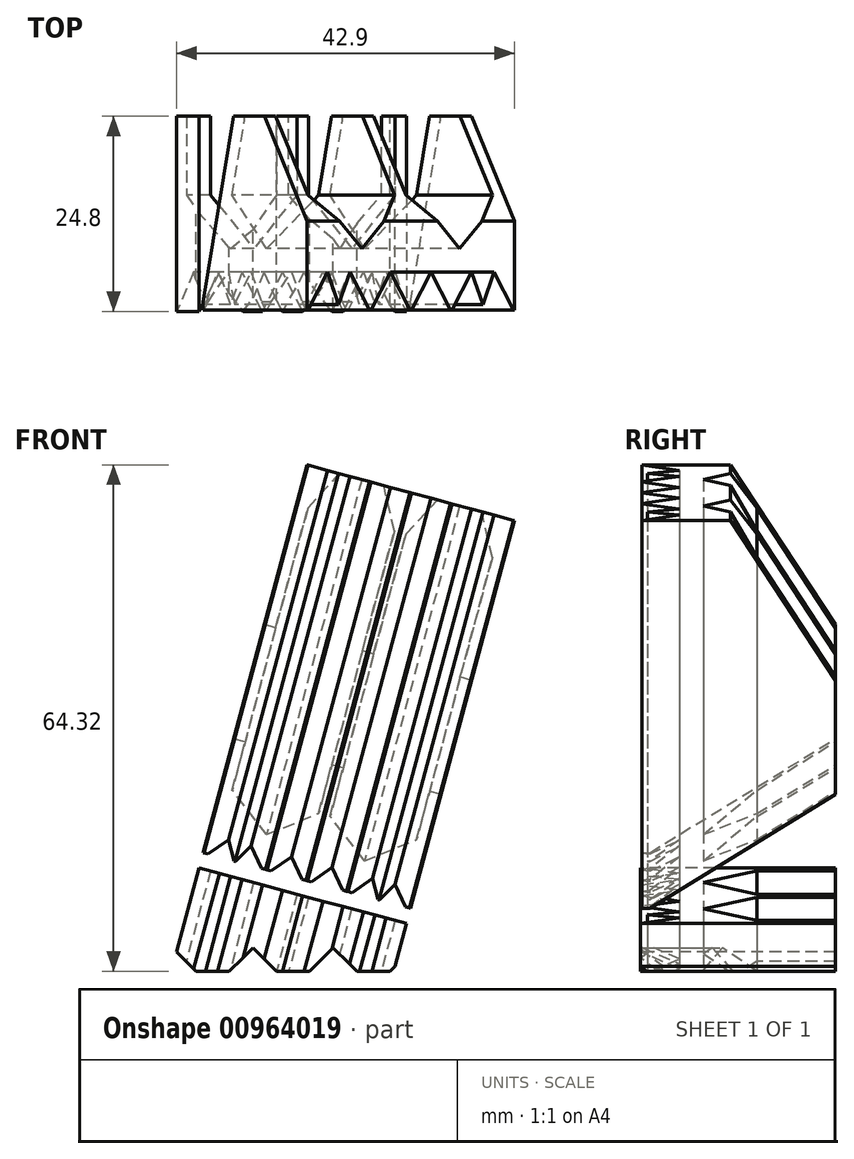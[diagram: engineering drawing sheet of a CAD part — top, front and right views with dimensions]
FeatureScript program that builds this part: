
annotation { "Feature Type Name" : "Feature", "Feature Type Description" : "" }
export const myFeature = defineFeature(function(context is Context, id is Id, definition is map)
    precondition{}
    {
        {
            assignVariable(context, id + "F0", {"variableType" : VariableType.LENGTH, "name" : "l", "lengthValue" : 35.5 * mm});
        }
        {
            assignVariable(context, id + "F1", {"variableType" : VariableType.LENGTH, "name" : "b", "lengthValue" : 23.6 * mm});
        }
        {
            assignVariable(context, id + "F2", {"variableType" : VariableType.LENGTH, "name" : "h", "lengthValue" : 50 * mm});
        }
        {
            var Q0;
            Q0=qCreatedBy(makeId("Front.planeOp"),FACE);
            var sketch = newSketch(context, id + "F3", { "sketchPlane" : qUnion([Q0])});
            skLineSegment(sketch, "E0", {"start": v(-22.52, 0) * mm, "end": v(-6.84, 58.52) * mm});
            skLineSegment(sketch, "E1", {"start": v(-6.84, 58.52) * mm, "end": v(35.18, 47.26) * mm});
            skLineSegment(sketch, "E2", {"start": v(35.18, 47.26) * mm, "end": v(22.52, 0) * mm});
            skLineSegment(sketch, "E3", {"start": v(22.52, 0) * mm, "end": v(22.52, -5) * mm});
            skLineSegment(sketch, "E4", {"start": v(15.31, -2) * mm, "end": v(12.31, -5) * mm});
            skLineSegment(sketch, "E5", {"start": v(15.31, -2) * mm, "end": v(18.31, -5) * mm});
            skLineSegment(sketch, "E6", {"start": v(14.17, 52.9) * mm, "end": v(0, 0) * mm, "construction": true});
            skLineSegment(sketch, "E7", {"start": v(-2.97, 57.48) * mm, "end": v(-15.91, 9.19) * mm, "construction": true});
            skLineSegment(sketch, "E8", {"start": v(-15.91, 9.19) * mm, "end": v(18.38, 0) * mm, "construction": true});
            skLineSegment(sketch, "E9", {"start": v(18.38, 0) * mm, "end": v(31.32, 48.3) * mm, "construction": true});
            skLineSegment(sketch, "E10", {"start": v(18.31, -5) * mm, "end": v(22.52, -5) * mm});
            skLineSegment(sketch, "E11", {"start": v(12.31, -5) * mm, "end": v(8.1, -5) * mm});
            skLineSegment(sketch, "E12.1.0.0", {"start": v(2.1, -5) * mm, "end": v(-2.1, -5) * mm});
            skLineSegment(sketch, "E12.1.0.1", {"start": v(5.1, -2) * mm, "end": v(8.1, -5) * mm});
            skLineSegment(sketch, "E12.1.0.2", {"start": v(5.1, -2) * mm, "end": v(2.1, -5) * mm});
            skLineSegment(sketch, "E12.2.0.0", {"start": v(-8.1, -5) * mm, "end": v(-12.31, -5) * mm});
            skLineSegment(sketch, "E12.2.0.1", {"start": v(-5.1, -2) * mm, "end": v(-2.1, -5) * mm});
            skLineSegment(sketch, "E12.2.0.2", {"start": v(-5.1, -2) * mm, "end": v(-8.1, -5) * mm});
            skLineSegment(sketch, "E12.3.0.0", {"start": v(-18.31, -5) * mm, "end": v(-22.52, -5) * mm});
            skLineSegment(sketch, "E12.3.0.1", {"start": v(-15.31, -2) * mm, "end": v(-12.31, -5) * mm});
            skLineSegment(sketch, "E12.3.0.2", {"start": v(-15.31, -2) * mm, "end": v(-18.31, -5) * mm});
            skLineSegment(sketch, "E12.direction1", {"start": v(8.1, -5) * mm, "end": v(-2.1, -5) * mm, "construction": true});
            skLineSegment(sketch, "E13", {"start": v(-22.52, -5) * mm, "end": v(-22.52, 0) * mm});
            skPoint(sketch, "E14", {"position": v(24.85, 24.15) * mm});
            skSolve(sketch);
        }
        {
            var Q0;
            Q0=sQuery(id+"F3.wireOp",EDGE,"E9");
            var Q1;
            Q1=sQuery(id+"F3.wireOp",VERTEX,"E14");
            cPlane(context, id + "F4", {"entities" : qUnion([Q0, Q1]), "cplaneType" : CPlaneType.LINE_POINT, "offset" : 25 * mm, "width" : 150 * mm, "height" : 150 * mm});
        }
        {
            var Q0;
            Q0=qCreatedBy(id+"F4.planeOp",FACE);
            var sketch = newSketch(context, id + "F5", { "sketchPlane" : qUnion([Q0])});
            skLineSegment(sketch, "E15.bottom", {"start": v(-17.75, 11.8) * mm, "end": v(17.75, 11.8) * mm, "construction": true});
            skLineSegment(sketch, "E15.top", {"start": v(-17.75, -11.8) * mm, "end": v(17.75, -11.8) * mm, "construction": true});
            skLineSegment(sketch, "E15.left", {"start": v(-17.75, 11.8) * mm, "end": v(-17.75, -11.8) * mm, "construction": true});
            skLineSegment(sketch, "E15.right", {"start": v(17.75, 11.8) * mm, "end": v(17.75, -11.8) * mm, "construction": true});
            skLineSegment(sketch, "E16.0", {"start": v(-18.35, 12.4) * mm, "end": v(18.35, 12.4) * mm});
            skLineSegment(sketch, "E16.1", {"start": v(-18.35, 12.4) * mm, "end": v(-18.35, -12.4) * mm});
            skLineSegment(sketch, "E16.2", {"start": v(-18.35, -12.4) * mm, "end": v(18.35, -12.4) * mm});
            skLineSegment(sketch, "E16.3", {"start": v(18.35, 12.4) * mm, "end": v(18.35, -12.4) * mm});
            skLineSegment(sketch, "E17", {"start": v(8.86, 12.4) * mm, "end": v(9.38, 11.5) * mm});
            skLineSegment(sketch, "E18", {"start": v(9.38, 11.5) * mm, "end": v(9.58, 11.5) * mm});
            skLineSegment(sketch, "E19", {"start": v(9.58, 11.5) * mm, "end": v(10.1, 12.4) * mm});
            skLineSegment(sketch, "E20", {"start": v(10.1, 12.4) * mm, "end": v(8.86, 12.4) * mm});
            skLineSegment(sketch, "E21", {"start": v(9.48, 12.4) * mm, "end": v(9.48, 11.5) * mm, "construction": true});
            skLineSegment(sketch, "E22.1.0", {"start": v(18.35, 7.12) * mm, "end": v(17.45, 6.6) * mm});
            skLineSegment(sketch, "E22.1.1", {"start": v(18.35, 6.5) * mm, "end": v(17.45, 6.5) * mm, "construction": true});
            skLineSegment(sketch, "E22.1.2", {"start": v(18.35, 5.88) * mm, "end": v(18.35, 7.12) * mm});
            skLineSegment(sketch, "E22.1.3", {"start": v(17.45, 6.4) * mm, "end": v(18.35, 5.88) * mm});
            skLineSegment(sketch, "E22.1.4", {"start": v(17.45, 6.6) * mm, "end": v(17.45, 6.4) * mm});
            skPoint(sketch, "E22.center", {"position": v(10.96, 5.01) * mm});
            skLineSegment(sketch, "E22.anchor1", {"start": v(10.96, 5.01) * mm, "end": v(9.48, 11.5) * mm, "construction": true});
            skLineSegment(sketch, "E22.anchor2", {"start": v(10.96, 5.01) * mm, "end": v(17.45, 6.5) * mm, "construction": true});
            skLineSegment(sketch, "E23.MirrorCS", {"start": v(9.38, -11.5) * mm, "end": v(9.58, -11.5) * mm});
            skLineSegment(sketch, "E24.MirrorCS", {"start": v(9.58, -11.5) * mm, "end": v(10.1, -12.4) * mm});
            skLineSegment(sketch, "E25.MirrorCS", {"start": v(10.1, -12.4) * mm, "end": v(8.86, -12.4) * mm});
            skLineSegment(sketch, "E26.MirrorCS", {"start": v(8.86, -12.4) * mm, "end": v(9.38, -11.5) * mm});
            skLineSegment(sketch, "E27.MirrorCS", {"start": v(9.48, -12.4) * mm, "end": v(9.48, -11.5) * mm, "construction": true});
            skLineSegment(sketch, "E28.MirrorCS", {"start": v(17.45, -6.6) * mm, "end": v(17.45, -6.4) * mm});
            skLineSegment(sketch, "E29.MirrorCS", {"start": v(18.35, -5.88) * mm, "end": v(18.35, -7.12) * mm});
            skLineSegment(sketch, "E30.MirrorCS", {"start": v(18.35, -6.5) * mm, "end": v(17.45, -6.5) * mm, "construction": true});
            skLineSegment(sketch, "E31.MirrorCS", {"start": v(18.35, -7.12) * mm, "end": v(17.45, -6.6) * mm});
            skLineSegment(sketch, "E32.MirrorCS", {"start": v(17.45, -6.4) * mm, "end": v(18.35, -5.88) * mm});
            skLineSegment(sketch, "E33", {"start": v(0, 11.8) * mm, "end": v(0, -11.8) * mm, "construction": true});
            skLineSegment(sketch, "E34.MirrorCS", {"start": v(-9.38, 11.5) * mm, "end": v(-9.58, 11.5) * mm});
            skLineSegment(sketch, "E35.MirrorCS", {"start": v(-9.57, 11.5) * mm, "end": v(-10.1, 12.4) * mm});
            skLineSegment(sketch, "E36.MirrorCS", {"start": v(-8.86, 12.4) * mm, "end": v(-9.38, 11.5) * mm});
            skLineSegment(sketch, "E37.MirrorCS", {"start": v(-9.47, 12.4) * mm, "end": v(-9.47, 11.5) * mm, "construction": true});
            skLineSegment(sketch, "E38.MirrorCS", {"start": v(-10.1, 12.4) * mm, "end": v(-8.86, 12.4) * mm});
            skLineSegment(sketch, "E39.MirrorCS", {"start": v(-17.45, 6.6) * mm, "end": v(-17.45, 6.4) * mm});
            skLineSegment(sketch, "E40.MirrorCS", {"start": v(-17.45, 6.4) * mm, "end": v(-18.35, 5.88) * mm});
            skLineSegment(sketch, "E41.MirrorCS", {"start": v(-18.35, 7.12) * mm, "end": v(-17.45, 6.6) * mm});
            skLineSegment(sketch, "E42.MirrorCS", {"start": v(-17.45, -6.6) * mm, "end": v(-17.45, -6.4) * mm});
            skLineSegment(sketch, "E43.MirrorCS", {"start": v(-17.45, -6.4) * mm, "end": v(-18.35, -5.88) * mm});
            skLineSegment(sketch, "E44.MirrorCS", {"start": v(-18.35, -7.12) * mm, "end": v(-17.45, -6.6) * mm});
            skLineSegment(sketch, "E45.MirrorCS", {"start": v(-18.35, 6.5) * mm, "end": v(-17.45, 6.5) * mm, "construction": true});
            skLineSegment(sketch, "E46.MirrorCS", {"start": v(-18.35, 5.88) * mm, "end": v(-18.35, 7.12) * mm});
            skLineSegment(sketch, "E47.MirrorCS", {"start": v(-18.35, -5.88) * mm, "end": v(-18.35, -7.12) * mm});
            skLineSegment(sketch, "E48.MirrorCS", {"start": v(-18.35, -6.5) * mm, "end": v(-17.45, -6.5) * mm, "construction": true});
            skLineSegment(sketch, "E49.MirrorCS", {"start": v(-9.38, -11.5) * mm, "end": v(-9.58, -11.5) * mm});
            skLineSegment(sketch, "E50.MirrorCS", {"start": v(-9.57, -11.5) * mm, "end": v(-10.1, -12.4) * mm});
            skLineSegment(sketch, "E51.MirrorCS", {"start": v(-9.48, -12.4) * mm, "end": v(-9.48, -11.5) * mm, "construction": true});
            skLineSegment(sketch, "E52.MirrorCS", {"start": v(-8.86, -12.4) * mm, "end": v(-9.38, -11.5) * mm});
            skLineSegment(sketch, "E53.MirrorCS", {"start": v(-10.1, -12.4) * mm, "end": v(-8.86, -12.4) * mm});
            skSolve(sketch);
        }
        {
            var Q0;
            Q0 = qSketchRegion(id + "F3", true);
            extrude(context, id + "F6", {"entities" : qUnion([Q0]), "depth" : getVariable(context, 'b') + 2 * 4 * mm, "offsetDistance" : 25 * mm, "symmetric" : true});
        }
        {
            var Q0;
            Q0 = qSketchRegion(id + "F5", true);
            extrude(context, id + "F7", {"entities" : qUnion([Q0]), "operationType" : NewBodyOperationType.REMOVE, "oppositeDirection" : true, "depth" : getVariable(context, 'h'), "offsetDistance" : 25 * mm, "symmetric" : true});
        }
        {
            var Q0;
            Q0=makeQuery(id+"F5.imprint","IMPRINT",FACE,{"disambiguationData":[TD([[makeQuery(id+"F5.imprint","IMPRINT",EDGE,{"derivedFrom":sQuery(id+"F5.wireOp",EDGE,"E49.MirrorCS")}),1.0]])]});
            var Q1;
            Q1=makeQuery(id+"F5.imprint","IMPRINT",FACE,{"disambiguationData":[TD([[makeQuery(id+"F5.imprint","IMPRINT",EDGE,{"derivedFrom":sQuery(id+"F5.wireOp",EDGE,"E23.MirrorCS")}),-1.0]])]});
            var Q2;
            Q2=makeQuery(id+"F5.imprint","IMPRINT",FACE,{"disambiguationData":[TD([[makeQuery(id+"F5.imprint","IMPRINT",EDGE,{"derivedFrom":sQuery(id+"F5.wireOp",EDGE,"E28.MirrorCS")}),-1.0]])]});
            var Q3;
            Q3=makeQuery(id+"F5.imprint","IMPRINT",FACE,{"disambiguationData":[TD([[makeQuery(id+"F5.imprint","IMPRINT",EDGE,{"derivedFrom":sQuery(id+"F5.wireOp",EDGE,"E42.MirrorCS")}),1.0]])]});
            var Q4;
            Q4=makeQuery(id+"F5.imprint","IMPRINT",FACE,{"disambiguationData":[TD([[makeQuery(id+"F5.imprint","IMPRINT",EDGE,{"derivedFrom":sQuery(id+"F5.wireOp",EDGE,"E39.MirrorCS")}),-1.0]])]});
            var Q5;
            Q5=makeQuery(id+"F5.imprint","IMPRINT",FACE,{"disambiguationData":[TD([[makeQuery(id+"F5.imprint","IMPRINT",EDGE,{"derivedFrom":sQuery(id+"F5.wireOp",EDGE,"E34.MirrorCS")}),-1.0]])]});
            var Q6;
            {var subQ0=sQuery(id+"F5.wireOp",EDGE,"E17");Q6=makeQuery(id+"F5.imprint","IMPRINT",FACE,{"disambiguationData":[TD([[makeQuery(id+"F5.imprint","IMPRINT",EDGE,{"derivedFrom":subQ0}),1.0]])]});}
            var Q7;
            {var subQ2=sQuery(id+"F5.wireOp",EDGE,"E22.1.0");Q7=makeQuery(id+"F5.imprint","IMPRINT",FACE,{"disambiguationData":[TD([[makeQuery(id+"F5.imprint","IMPRINT",EDGE,{"derivedFrom":subQ2}),1.0]])]});}
            extrude(context, id + "F8", {"entities" : qUnion([Q0, Q1, Q2, Q3, Q4, Q5, Q6, Q7]), "operationType" : NewBodyOperationType.ADD, "depth" : getVariable(context, 'h') / 3, "offsetDistance" : 25 * mm, "hasSecondDirection" : true, "secondDirectionOppositeDirection" : true, "secondDirectionDepth" : getVariable(context, 'h') / 2 - 2 * mm});
        }
        {
            var Q0;
            Q0=makeQuery(id+"F8.opExtrude","CAP_EDGE",EDGE,{"disambiguationData":[OSD([sQuery(id+"F5.wireOp",EDGE,"E34.MirrorCS")])],"isStart":false});
            var Q1;
            Q1=makeQuery(id+"F8.opExtrude","CAP_EDGE",EDGE,{"disambiguationData":[OSD([sQuery(id+"F5.wireOp",EDGE,"E28.MirrorCS")])],"isStart":false});
            var Q2;
            Q2=makeQuery(id+"F8.opExtrude","CAP_EDGE",EDGE,{"disambiguationData":[OSD([sQuery(id+"F5.wireOp",EDGE,"E23.MirrorCS")])],"isStart":false});
            var Q3;
            Q3=makeQuery(id+"F8.opExtrude","CAP_EDGE",EDGE,{"disambiguationData":[OSD([sQuery(id+"F5.wireOp",EDGE,"E39.MirrorCS")])],"isStart":false});
            chamfer(context, id + "F9", {"entities" : qUnion([Q0, Q1, Q2, Q3]), "chamferType" : ChamferType.OFFSET_ANGLE, "width" : 3 * mm, "oppositeDirection" : false, "angle" : 20 * degree});
        }
        {
            var Q0;
            Q0=makeQuery(id+"F8.opExtrude","CAP_EDGE",EDGE,{"disambiguationData":[OSD([sQuery(id+"F5.wireOp",EDGE,"E42.MirrorCS")])],"isStart":false});
            var Q1;
            Q1=makeQuery(id+"F8.opExtrude","CAP_EDGE",EDGE,{"disambiguationData":[OSD([sQuery(id+"F5.wireOp",EDGE,"E49.MirrorCS")])],"isStart":false});
            var Q2;
            Q2=makeQuery(id+"F8.opExtrude","CAP_EDGE",EDGE,{"disambiguationData":[OSD([sQuery(id+"F5.wireOp",EDGE,"E18")])],"isStart":false});
            var Q3;
            Q3=makeQuery(id+"F8.opExtrude","CAP_EDGE",EDGE,{"disambiguationData":[OSD([sQuery(id+"F5.wireOp",EDGE,"E22.1.4")])],"isStart":false});
            chamfer(context, id + "F10", {"entities" : qUnion([Q0, Q1, Q2, Q3]), "chamferType" : ChamferType.OFFSET_ANGLE, "width" : 1 * mm, "oppositeDirection" : false, "angle" : 70 * degree, "tangentPropagation" : true});
        }
        {
            var Q0;
            Q0=makeQuery(id+"F6.opExtrude","SWEPT_FACE",FACE,{"disambiguationData":[OSD([sQuery(id+"F3.wireOp",EDGE,"E1")])]});
            chamfer(context, id + "F11", {"entities" : qUnion([Q0]), "width" : 1 * mm, "tangentPropagation" : true});
        }
        {
            var Q0;
            Q0=makeQuery(id+"F6.opExtrude","CAP_EDGE",EDGE,{"disambiguationData":[OSD([sQuery(id+"F3.wireOp",EDGE,"E0")])],"isStart":false});
            var Q1;
            Q1=makeQuery(id+"F6.opExtrude","CAP_EDGE",EDGE,{"disambiguationData":[OSD([sQuery(id+"F3.wireOp",EDGE,"E0")])],"isStart":true});
            var Q2;
            Q2=makeQuery(id+"F6.opExtrude","CAP_EDGE",EDGE,{"disambiguationData":[OSD([sQuery(id+"F3.wireOp",EDGE,"E2")])],"isStart":false});
            var Q3;
            Q3=makeQuery(id+"F6.opExtrude","CAP_EDGE",EDGE,{"disambiguationData":[OSD([sQuery(id+"F3.wireOp",EDGE,"E2")])],"isStart":true});
            var Q4;
            Q4=makeQuery(id+"F6.opExtrude","CAP_EDGE",EDGE,{"disambiguationData":[OSD([sQuery(id+"F3.wireOp",EDGE,"E3")])],"isStart":false});
            var Q5;
            Q5=makeQuery(id+"F6.opExtrude","CAP_EDGE",EDGE,{"disambiguationData":[OSD([sQuery(id+"F3.wireOp",EDGE,"E3")])],"isStart":true});
            var Q6;
            Q6=makeQuery(id+"F6.opExtrude","CAP_EDGE",EDGE,{"disambiguationData":[OSD([sQuery(id+"F3.wireOp",EDGE,"E13")])],"isStart":false});
            var Q7;
            Q7=makeQuery(id+"F6.opExtrude","CAP_EDGE",EDGE,{"disambiguationData":[OSD([sQuery(id+"F3.wireOp",EDGE,"E13")])],"isStart":true});
            var Q8;
            Q8=makeQuery(id+"F6.opExtrude","CAP_EDGE",EDGE,{"disambiguationData":[OSD([sQuery(id+"F3.wireOp",EDGE,"E12.3.0.0")])],"isStart":false});
            var Q9;
            Q9=makeQuery(id+"F6.opExtrude","CAP_EDGE",EDGE,{"disambiguationData":[OSD([sQuery(id+"F3.wireOp",EDGE,"E12.2.0.0")])],"isStart":false});
            var Q10;
            Q10=makeQuery(id+"F6.opExtrude","CAP_EDGE",EDGE,{"disambiguationData":[OSD([sQuery(id+"F3.wireOp",EDGE,"E12.3.0.1")])],"isStart":false});
            var Q11;
            Q11=makeQuery(id+"F6.opExtrude","CAP_EDGE",EDGE,{"disambiguationData":[OSD([sQuery(id+"F3.wireOp",EDGE,"E12.3.0.2")])],"isStart":false});
            var Q12;
            Q12=makeQuery(id+"F6.opExtrude","CAP_EDGE",EDGE,{"disambiguationData":[OSD([sQuery(id+"F3.wireOp",EDGE,"E12.2.0.2")])],"isStart":false});
            var Q13;
            Q13=makeQuery(id+"F6.opExtrude","CAP_EDGE",EDGE,{"disambiguationData":[OSD([sQuery(id+"F3.wireOp",EDGE,"E12.2.0.1")])],"isStart":false});
            var Q14;
            Q14=makeQuery(id+"F6.opExtrude","CAP_EDGE",EDGE,{"disambiguationData":[OSD([sQuery(id+"F3.wireOp",EDGE,"E12.1.0.0")])],"isStart":false});
            var Q15;
            Q15=makeQuery(id+"F6.opExtrude","CAP_EDGE",EDGE,{"disambiguationData":[OSD([sQuery(id+"F3.wireOp",EDGE,"E12.1.0.2")])],"isStart":false});
            var Q16;
            Q16=makeQuery(id+"F6.opExtrude","CAP_EDGE",EDGE,{"disambiguationData":[OSD([sQuery(id+"F3.wireOp",EDGE,"E12.1.0.1")])],"isStart":false});
            var Q17;
            Q17=makeQuery(id+"F6.opExtrude","CAP_EDGE",EDGE,{"disambiguationData":[OSD([sQuery(id+"F3.wireOp",EDGE,"E11")])],"isStart":false});
            var Q18;
            Q18=makeQuery(id+"F6.opExtrude","CAP_EDGE",EDGE,{"disambiguationData":[OSD([sQuery(id+"F3.wireOp",EDGE,"E4")])],"isStart":false});
            var Q19;
            Q19=makeQuery(id+"F6.opExtrude","CAP_EDGE",EDGE,{"disambiguationData":[OSD([sQuery(id+"F3.wireOp",EDGE,"E5")])],"isStart":false});
            var Q20;
            Q20=makeQuery(id+"F6.opExtrude","CAP_EDGE",EDGE,{"disambiguationData":[OSD([sQuery(id+"F3.wireOp",EDGE,"E10")])],"isStart":false});
            var Q21;
            Q21=makeQuery(id+"F6.opExtrude","CAP_EDGE",EDGE,{"disambiguationData":[OSD([sQuery(id+"F3.wireOp",EDGE,"E10")])],"isStart":true});
            var Q22;
            Q22=makeQuery(id+"F6.opExtrude","CAP_EDGE",EDGE,{"disambiguationData":[OSD([sQuery(id+"F3.wireOp",EDGE,"E5")])],"isStart":true});
            var Q23;
            Q23=makeQuery(id+"F6.opExtrude","CAP_EDGE",EDGE,{"disambiguationData":[OSD([sQuery(id+"F3.wireOp",EDGE,"E4")])],"isStart":true});
            var Q24;
            Q24=makeQuery(id+"F6.opExtrude","CAP_EDGE",EDGE,{"disambiguationData":[OSD([sQuery(id+"F3.wireOp",EDGE,"E11")])],"isStart":true});
            var Q25;
            Q25=makeQuery(id+"F6.opExtrude","CAP_EDGE",EDGE,{"disambiguationData":[OSD([sQuery(id+"F3.wireOp",EDGE,"E12.1.0.1")])],"isStart":true});
            var Q26;
            Q26=makeQuery(id+"F6.opExtrude","CAP_EDGE",EDGE,{"disambiguationData":[OSD([sQuery(id+"F3.wireOp",EDGE,"E12.1.0.2")])],"isStart":true});
            var Q27;
            Q27=makeQuery(id+"F6.opExtrude","CAP_EDGE",EDGE,{"disambiguationData":[OSD([sQuery(id+"F3.wireOp",EDGE,"E12.1.0.0")])],"isStart":true});
            var Q28;
            Q28=makeQuery(id+"F6.opExtrude","CAP_EDGE",EDGE,{"disambiguationData":[OSD([sQuery(id+"F3.wireOp",EDGE,"E12.2.0.1")])],"isStart":true});
            var Q29;
            Q29=makeQuery(id+"F6.opExtrude","CAP_EDGE",EDGE,{"disambiguationData":[OSD([sQuery(id+"F3.wireOp",EDGE,"E12.2.0.2")])],"isStart":true});
            var Q30;
            Q30=makeQuery(id+"F6.opExtrude","CAP_EDGE",EDGE,{"disambiguationData":[OSD([sQuery(id+"F3.wireOp",EDGE,"E12.2.0.0")])],"isStart":true});
            var Q31;
            Q31=makeQuery(id+"F6.opExtrude","CAP_EDGE",EDGE,{"disambiguationData":[OSD([sQuery(id+"F3.wireOp",EDGE,"E12.3.0.1")])],"isStart":true});
            var Q32;
            Q32=makeQuery(id+"F6.opExtrude","CAP_EDGE",EDGE,{"disambiguationData":[OSD([sQuery(id+"F3.wireOp",EDGE,"E12.3.0.2")])],"isStart":true});
            var Q33;
            Q33=makeQuery(id+"F6.opExtrude","CAP_EDGE",EDGE,{"disambiguationData":[OSD([sQuery(id+"F3.wireOp",EDGE,"E12.3.0.0")])],"isStart":true});
            chamfer(context, id + "F12", {"entities" : qUnion([Q0, Q1, Q2, Q3, Q4, Q5, Q6, Q7, Q8, Q9, Q10, Q11, Q12, Q13, Q14, Q15, Q16, Q17, Q18, Q19, Q20, Q21, Q22, Q23, Q24, Q25, Q26, Q27, Q28, Q29, Q30, Q31, Q32, Q33]), "width" : 2 * mm, "tangentPropagation" : true});
        }
        {
            var Q0;
            Q0=qCreatedBy(makeId("Front.planeOp"),FACE);
            var sketch = newSketch(context, id + "F13", { "sketchPlane" : qUnion([Q0])});
            skLineSegment(sketch, "E54", {"start": v(-9.24, 41.82) * mm, "end": v(-8.48, 33.08) * mm});
            skLineSegment(sketch, "E55", {"start": v(-8.48, 33.08) * mm, "end": v(-9.23, 30.25) * mm});
            skLineSegment(sketch, "E56", {"start": v(-9.23, 30.25) * mm, "end": v(-10, 39) * mm});
            skLineSegment(sketch, "E57", {"start": v(-10, 39) * mm, "end": v(-9.24, 41.82) * mm});
            skLineSegment(sketch, "E58", {"start": v(-10, 39) * mm, "end": v(-12.27, 30.52) * mm});
            skLineSegment(sketch, "E59", {"start": v(-12.27, 30.52) * mm, "end": v(-9.37, 29.74) * mm});
            skLineSegment(sketch, "E60", {"start": v(-9.37, 29.74) * mm, "end": v(-9.23, 30.25) * mm});
            skLineSegment(sketch, "E61.MirrorCS", {"start": v(22.99, 21.07) * mm, "end": v(23.12, 21.58) * mm});
            skLineSegment(sketch, "E62.MirrorCS", {"start": v(28.16, 28.77) * mm, "end": v(25.88, 20.3) * mm});
            skLineSegment(sketch, "E63.MirrorCS", {"start": v(25.88, 20.3) * mm, "end": v(22.99, 21.07) * mm});
            skLineSegment(sketch, "E64.MirrorCS", {"start": v(23.12, 21.58) * mm, "end": v(28.16, 28.77) * mm});
            skLineSegment(sketch, "E65.MirrorCS", {"start": v(28.91, 31.6) * mm, "end": v(23.88, 24.4) * mm});
            skLineSegment(sketch, "E66.MirrorCS", {"start": v(23.88, 24.4) * mm, "end": v(23.12, 21.58) * mm});
            skLineSegment(sketch, "E67.MirrorCS", {"start": v(28.16, 28.77) * mm, "end": v(28.91, 31.6) * mm});
            skSolve(sketch);
        }
        {
            var Q0;
            Q0=makeQuery(id+"F7.boolean.opBoolean","COPY",FACE,{"derivedFrom":makeQuery(id+"F7.opExtrude","CAP_FACE",FACE,{"disambiguationData":[OSD([sQuery(id+"F5.wireOp",EDGE,"E16.0"),sQuery(id+"F5.wireOp",EDGE,"E16.1"),sQuery(id+"F5.wireOp",EDGE,"E16.2"),sQuery(id+"F5.wireOp",EDGE,"E16.3")])],"isStart":false})});
            var sketch = newSketch(context, id + "F14", { "sketchPlane" : qUnion([Q0])});
            skCircle(sketch, "E68", {"center": v(15.3, 0) * mm, "radius": 2 * mm});
            skCircle(sketch, "E69", {"center": v(-14.27, 0) * mm, "radius": 2 * mm});
            skCircle(sketch, "E70", {"center": v(-4.41, 0) * mm, "radius": 2 * mm});
            skCircle(sketch, "E71", {"center": v(5.45, 0) * mm, "radius": 2 * mm});
            skSolve(sketch);
        }
        {
            var Q0;
            Q0=makeQuery(id+"F6.opExtrude","SWEPT_FACE",FACE,{"disambiguationData":[OSD([sQuery(id+"F3.wireOp",EDGE,"E2")])]});
            var Q1;
            Q1=makeQuery(id+"F6.opExtrude","SWEPT_FACE",FACE,{"disambiguationData":[OSD([sQuery(id+"F3.wireOp",EDGE,"E0")])]});
            cPlane(context, id + "F15", {"entities" : qUnion([Q0, Q1]), "cplaneType" : CPlaneType.MID_PLANE, "offset" : 25 * mm, "width" : 150 * mm, "height" : 150 * mm});
        }
        {
            var Q0;
            Q0=qCreatedBy(id+"F15.planeOp",FACE);
            var sketch = newSketch(context, id + "F16", { "sketchPlane" : qUnion([Q0])});
            skLineSegment(sketch, "E72", {"start": v(-12.2, 57.76) * mm, "end": v(-0.95, 57.76) * mm});
            skLineSegment(sketch, "E73", {"start": v(-0.95, 57.76) * mm, "end": v(12.4, 36.76) * mm});
            skLineSegment(sketch, "E74", {"start": v(12.4, 36.76) * mm, "end": v(12.4, 21.76) * mm});
            skLineSegment(sketch, "E75", {"start": v(12.4, 21.76) * mm, "end": v(-11.2, 6.76) * mm});
            skLineSegment(sketch, "E76", {"start": v(-11.2, 6.76) * mm, "end": v(-12.2, 6.76) * mm});
            skLineSegment(sketch, "E77", {"start": v(-12.2, 6.76) * mm, "end": v(-12.2, 57.76) * mm});
            skSolve(sketch);
        }
        {
            var Q0;
            Q0=qCreatedBy(id+"F4.planeOp",FACE);
            var sketch = newSketch(context, id + "F17", { "sketchPlane" : qUnion([Q0])});
            skLineSegment(sketch, "E78", {"start": v(-13.63, -12.4) * mm, "end": v(-13.63, 12.4) * mm});
            skLineSegment(sketch, "E79", {"start": v(-13.63, 12.4) * mm, "end": v(-12.13, 12.4) * mm});
            skLineSegment(sketch, "E80", {"start": v(-0.75, 12.4) * mm, "end": v(0.75, 12.4) * mm});
            skLineSegment(sketch, "E81.MirrorCS", {"start": v(13.63, 12.4) * mm, "end": v(12.13, 12.4) * mm});
            skLineSegment(sketch, "E82.MirrorCS", {"start": v(13.63, -12.4) * mm, "end": v(13.63, 12.4) * mm});
            skLineSegment(sketch, "E83", {"start": v(13.63, -12.4) * mm, "end": v(10.97, -7.4) * mm});
            skLineSegment(sketch, "E84", {"start": v(10.97, -7.4) * mm, "end": v(9.48, -11.5) * mm});
            skLineSegment(sketch, "E85", {"start": v(9.48, -11.5) * mm, "end": v(7.98, -7.4) * mm});
            skLineSegment(sketch, "E86", {"start": v(7.98, -7.4) * mm, "end": v(5.32, -12.4) * mm});
            skLineSegment(sketch, "E87", {"start": v(5.32, -12.4) * mm, "end": v(2.66, -7.4) * mm});
            skLineSegment(sketch, "E88", {"start": v(2.66, -7.4) * mm, "end": v(0, -12.4) * mm});
            skLineSegment(sketch, "E89.MirrorCS", {"start": v(-7.98, -7.4) * mm, "end": v(-5.32, -12.4) * mm});
            skLineSegment(sketch, "E90.MirrorCS", {"start": v(-5.32, -12.4) * mm, "end": v(-2.66, -7.4) * mm});
            skLineSegment(sketch, "E91.MirrorCS", {"start": v(-2.66, -7.4) * mm, "end": v(0, -12.4) * mm});
            skLineSegment(sketch, "E92.MirrorCS", {"start": v(-9.48, -11.5) * mm, "end": v(-7.98, -7.4) * mm});
            skLineSegment(sketch, "E93.MirrorCS", {"start": v(-10.97, -7.4) * mm, "end": v(-9.48, -11.5) * mm});
            skLineSegment(sketch, "E94.MirrorCS", {"start": v(-13.63, -12.4) * mm, "end": v(-10.97, -7.4) * mm});
            skLineSegment(sketch, "E95", {"start": v(6.44, -4.4) * mm, "end": v(0.75, 2.38) * mm});
            skLineSegment(sketch, "E96", {"start": v(0.75, 2.38) * mm, "end": v(0.75, 12.4) * mm});
            skLineSegment(sketch, "E97", {"start": v(6.44, -4.4) * mm, "end": v(12.13, 2.38) * mm});
            skLineSegment(sketch, "E98", {"start": v(12.13, 2.38) * mm, "end": v(12.13, 12.4) * mm});
            skLineSegment(sketch, "E99.MirrorCS", {"start": v(-0.75, 2.38) * mm, "end": v(-0.75, 12.4) * mm});
            skLineSegment(sketch, "E100.MirrorCS", {"start": v(-6.44, -4.4) * mm, "end": v(-12.13, 2.38) * mm});
            skLineSegment(sketch, "E101.MirrorCS", {"start": v(-12.13, 2.38) * mm, "end": v(-12.13, 12.4) * mm});
            skLineSegment(sketch, "E102.MirrorCS", {"start": v(-6.44, -4.4) * mm, "end": v(-0.75, 2.38) * mm});
            skSolve(sketch);
        }
        {
            var Q0;
            Q0 = qSketchRegion(id + "F16", true);
            extrude(context, id + "F18", {"entities" : qUnion([Q0]), "depth" : getVariable(context, 'l'), "offsetDistance" : 25 * mm, "symmetric" : true});
        }
        {
            var Q0;
            Q0 = qSketchRegion(id + "F17", true);
            extrude(context, id + "F19", {"entities" : qUnion([Q0]), "operationType" : NewBodyOperationType.INTERSECT, "depth" : 1000 * mm, "offsetDistance" : 25 * mm, "symmetric" : true});
        }
    });
